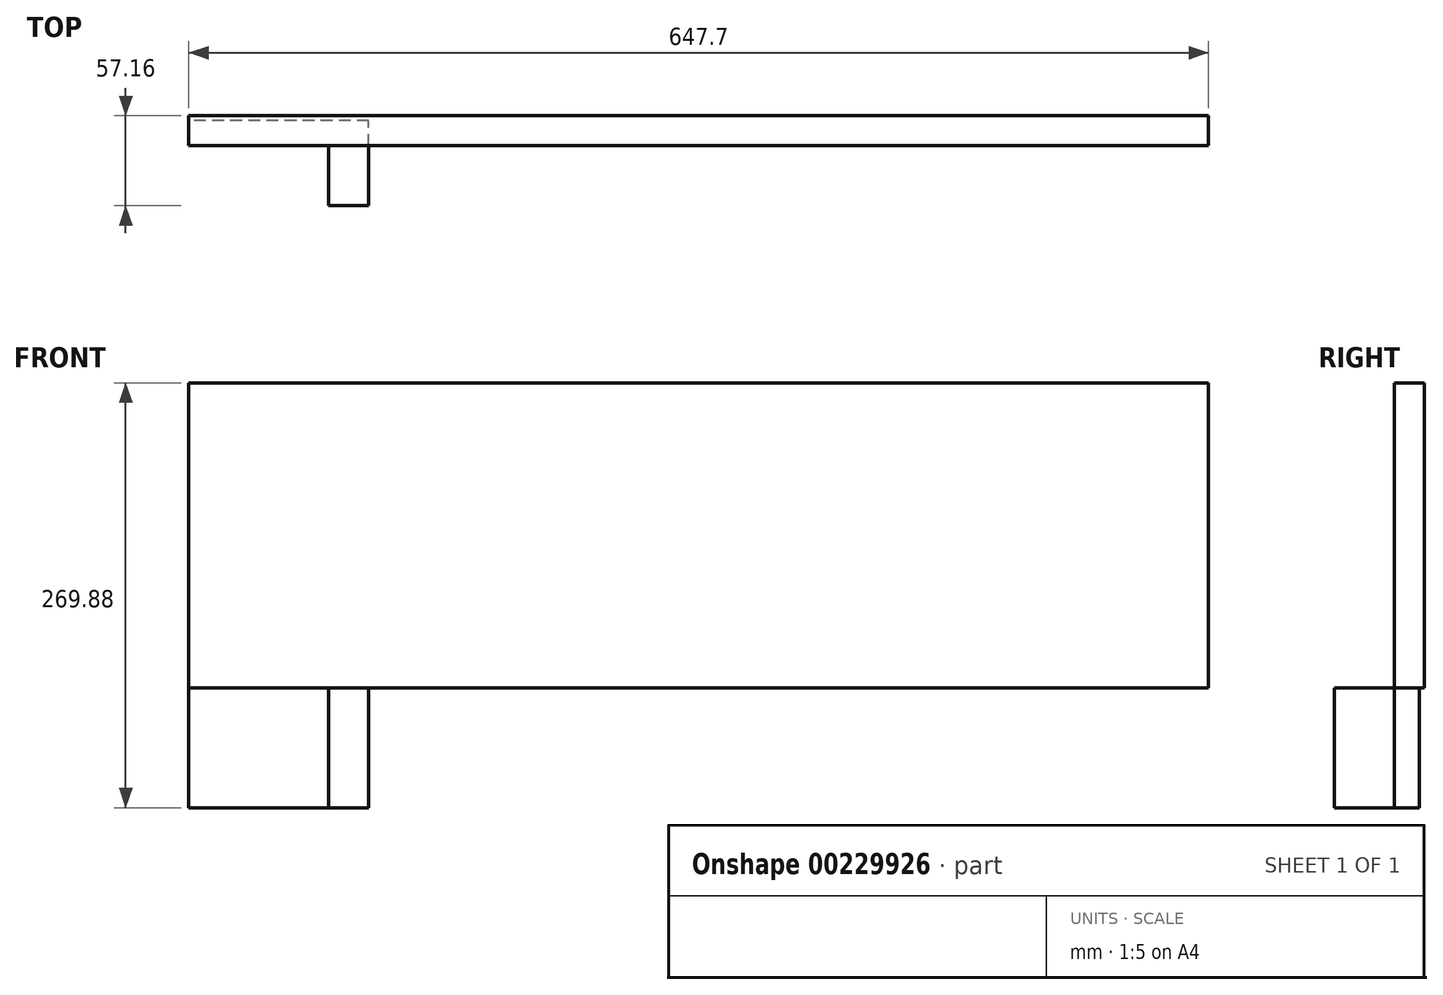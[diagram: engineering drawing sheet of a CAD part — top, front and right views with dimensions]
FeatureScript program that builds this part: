
annotation { "Feature Type Name" : "Feature", "Feature Type Description" : "" }
export const myFeature = defineFeature(function(context is Context, id is Id, definition is map)
    precondition{}
    {
        {
            var Q0;
            Q0=qCreatedBy(makeId("Front.planeOp"),FACE);
            var sketch = newSketch(context, id + "F0", { "sketchPlane" : qUnion([Q0])});
            skLineSegment(sketch, "E0.bottom", {"start": v(57.15, 38.1) * mm, "end": v(-57.15, 38.1) * mm});
            skLineSegment(sketch, "E0.top", {"start": v(57.15, -38.1) * mm, "end": v(-57.15, -38.1) * mm});
            skLineSegment(sketch, "E0.left", {"start": v(57.15, 38.1) * mm, "end": v(57.15, -38.1) * mm});
            skLineSegment(sketch, "E0.right", {"start": v(-57.15, 38.1) * mm, "end": v(-57.15, -38.1) * mm});
            skPoint(sketch, "E0.middle", {"position": v(0, 0) * mm});
            skSolve(sketch);
        }
        {
            var Q0;
            Q0 = qSketchRegion(id + "F0", true);
            extrude(context, id + "F1", {"entities" : qUnion([Q0]), "depth" : 15.88 * mm, "offsetDistance" : 25.4 * mm});
        }
        {
            var Q0;
            Q0=makeQuery(id+"F1.opExtrude","CAP_FACE",FACE,{"disambiguationData":[OSD([sQuery(id+"F0.wireOp",EDGE,"E0.bottom"),sQuery(id+"F0.wireOp",EDGE,"E0.top"),sQuery(id+"F0.wireOp",EDGE,"E0.left"),sQuery(id+"F0.wireOp",EDGE,"E0.right")])],"isStart":false});
            var sketch = newSketch(context, id + "F2", { "sketchPlane" : qUnion([Q0])});
            skLineSegment(sketch, "E1.bottom", {"start": v(57.15, 38.1) * mm, "end": v(31.75, 38.1) * mm});
            skLineSegment(sketch, "E1.top", {"start": v(57.15, -38.1) * mm, "end": v(31.75, -38.1) * mm});
            skLineSegment(sketch, "E1.left", {"start": v(57.15, 38.1) * mm, "end": v(57.15, -38.1) * mm});
            skLineSegment(sketch, "E1.right", {"start": v(31.75, 38.1) * mm, "end": v(31.75, -38.1) * mm});
            skSolve(sketch);
        }
        {
            var Q0;
            Q0 = qSketchRegion(id + "F2", true);
            extrude(context, id + "F3", {"entities" : qUnion([Q0]), "depth" : 38.1 * mm, "offsetDistance" : 25.4 * mm});
        }
        {
            var Q0;
            Q0=makeQuery(id+"F1.opExtrude","SWEPT_FACE",FACE,{"disambiguationData":[OSD([sQuery(id+"F0.wireOp",EDGE,"E0.right")])]});
            var sketch = newSketch(context, id + "F4", { "sketchPlane" : qUnion([Q0])});
            skLineSegment(sketch, "E2.bottom", {"start": v(15.87, 38.1) * mm, "end": v(-3.17, 38.1) * mm});
            skLineSegment(sketch, "E2.top", {"start": v(15.87, 231.78) * mm, "end": v(-3.18, 231.78) * mm});
            skLineSegment(sketch, "E2.left", {"start": v(15.88, 38.1) * mm, "end": v(15.88, 231.77) * mm});
            skLineSegment(sketch, "E2.right", {"start": v(-3.18, 38.1) * mm, "end": v(-3.18, 231.77) * mm});
            skSolve(sketch);
        }
        {
            var Q0;
            Q0 = qSketchRegion(id + "F4", true);
            extrude(context, id + "F5", {"entities" : qUnion([Q0]), "oppositeDirection" : true, "depth" : 647.7 * mm, "offsetDistance" : 25.4 * mm});
        }
    });
